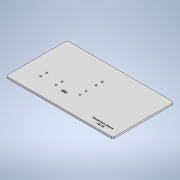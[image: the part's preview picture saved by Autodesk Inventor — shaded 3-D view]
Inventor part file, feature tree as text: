
AUTODESK INVENTOR PART (.ipt)
format: ipt  version: 2022 (Build 260153000, 153)  size: 139,264 bytes
history: native  units: mm
features: sketch x3, extrude x2, fillet x1, hole x1
ambient origin geometry x8: Origin, YZ Plane, XZ Plane, XY Plane, X Axis, Y Axis, Z Axis, Center Point
bodies: Solid1 (feature_tree)
feature tree (7):
  extrude  "Extrusion1"  Depth=200.0mm
  fillet  "Fillet1"  Radius=6.0mm
  sketch  "Sketch2"  dims[d4=5.0mm d7=20.0mm]
  sketch  "Sketch3"  dims[d8=20.0mm d11=5.4mm d12=6.0mm d13=4.0mm d14=2.0mm d15=90.0deg d16=8.0mm d17=20.594885mm d18=20.0mm d19=20.0mm d20=50.0mm d21=58.5mm d22=55.0mm d23=60.0mm d24=33.0mm d25=15.0mm d26=6.0mm d27=35.0mm d28=0.0mm d29=0.0mm d30=50.0mm]
  hole  "Hole1"  [1 undecoded]
  extrude  "Extrusion2"  Depth=6.0mm
  sketch  "Sketch1"  dims[d0=350.0mm d1=200.0mm d2=6.0mm d3=0.0mm]
note: 1 required parameter value undecoded (feature->parameter linkage not recoverable at this tier; creation-order binding heuristic only, values carry confidence <= 0.55)
